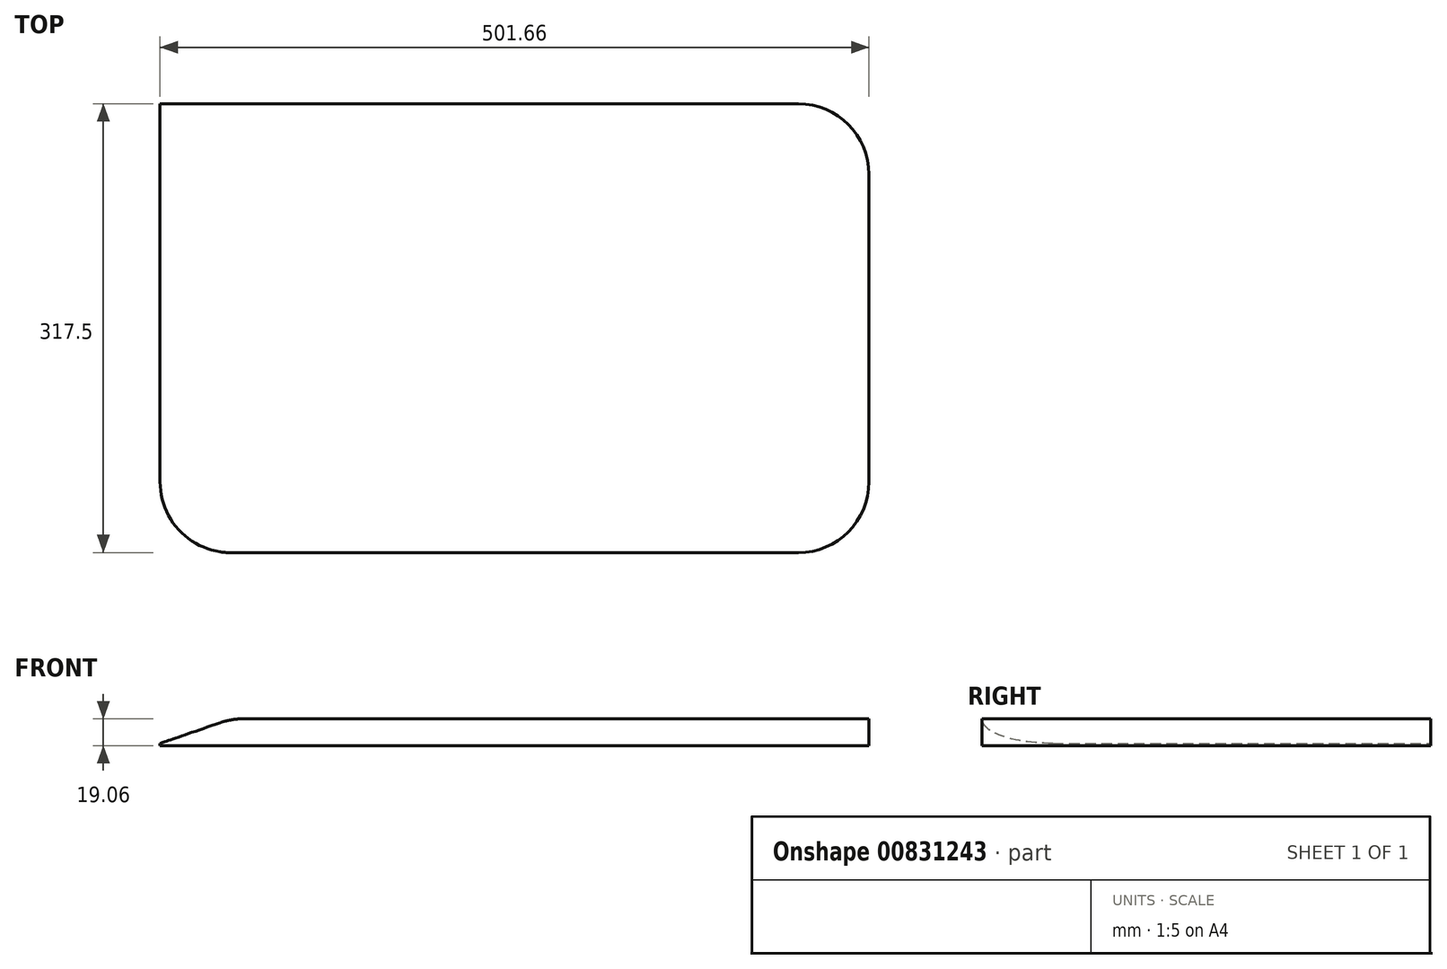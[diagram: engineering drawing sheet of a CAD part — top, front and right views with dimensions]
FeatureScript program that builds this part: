
annotation { "Feature Type Name" : "Feature", "Feature Type Description" : "" }
export const myFeature = defineFeature(function(context is Context, id is Id, definition is map)
    precondition{}
    {
        {
            var Q0;
            Q0=qCreatedBy(makeId("Front.planeOp"),FACE);
            var sketch = newSketch(context, id + "F0", { "sketchPlane" : qUnion([Q0])});
            skLineSegment(sketch, "E0.bottom", {"start": v(250.83, -9.52) * mm, "end": v(-250.83, -9.53) * mm});
            skLineSegment(sketch, "E0.top", {"start": v(250.83, 9.53) * mm, "end": v(-191.67, 9.52) * mm});
            skLineSegment(sketch, "E0.left", {"start": v(250.83, -9.52) * mm, "end": v(250.83, 9.53) * mm});
            skPoint(sketch, "E0.middle", {"position": v(0, 0) * mm});
            skLineSegment(sketch, "E1", {"start": v(-250.83, -9.53) * mm, "end": v(-250.83, -7.94) * mm});
            skLineSegment(sketch, "E2", {"start": v(-250.83, -9.53) * mm, "end": v(-200.02, -9.53) * mm});
            skLineSegment(sketch, "E3", {"start": v(-250.83, -7.94) * mm, "end": v(-208.23, 6.75) * mm});
            skPoint(sketch, "E4.orphan", {"position": v(-250.83, 9.52) * mm});
            skPoint(sketch, "E5.visualSharp", {"position": v(-200.18, 9.53) * mm});
            skArc(sketch, "E5.filletArc", {"start": v(-191.67, 9.53) * mm, "mid": v(-200.07, 8.83) * mm, "end": v(-208.23, 6.75) * mm});
            skSolve(sketch);
        }
        {
            var Q0;
            Q0=makeQuery(id+"F0.imprint","IMPRINT",FACE,{"disambiguationData":[TD([[makeQuery(id+"F0.imprint","IMPRINT",EDGE,{"derivedFrom":sQuery(id+"F0.wireOp",EDGE,"E0.bottom")}),-1.0]])]});
            extrude(context, id + "F1", {"entities" : qUnion([Q0]), "endBound" : BoundingType.SYMMETRIC, "depth" : 317.5 * mm, "offsetDistance" : 25.4 * mm});
        }
        {
            var Q0;
            Q0=makeQuery(id+"F1.opExtrude","CAP_EDGE",EDGE,{"disambiguationData":[OSD([sQuery(id+"F0.wireOp",EDGE,"E1")])],"isStart":false});
            var Q1;
            Q1=makeQuery(id+"F1.opExtrude","CAP_EDGE",EDGE,{"disambiguationData":[OSD([sQuery(id+"F0.wireOp",EDGE,"E0.left")])],"isStart":false});
            var Q2;
            Q2=makeQuery(id+"F1.opExtrude","CAP_EDGE",EDGE,{"disambiguationData":[OSD([sQuery(id+"F0.wireOp",EDGE,"E0.left")])],"isStart":true});
            fillet(context, id + "F2", {"entities" : qUnion([Q0, Q1, Q2]), "radius" : 50 * mm, "tangentPropagation" : true, "allowEdgeOverflow" : false});
        }
    });
